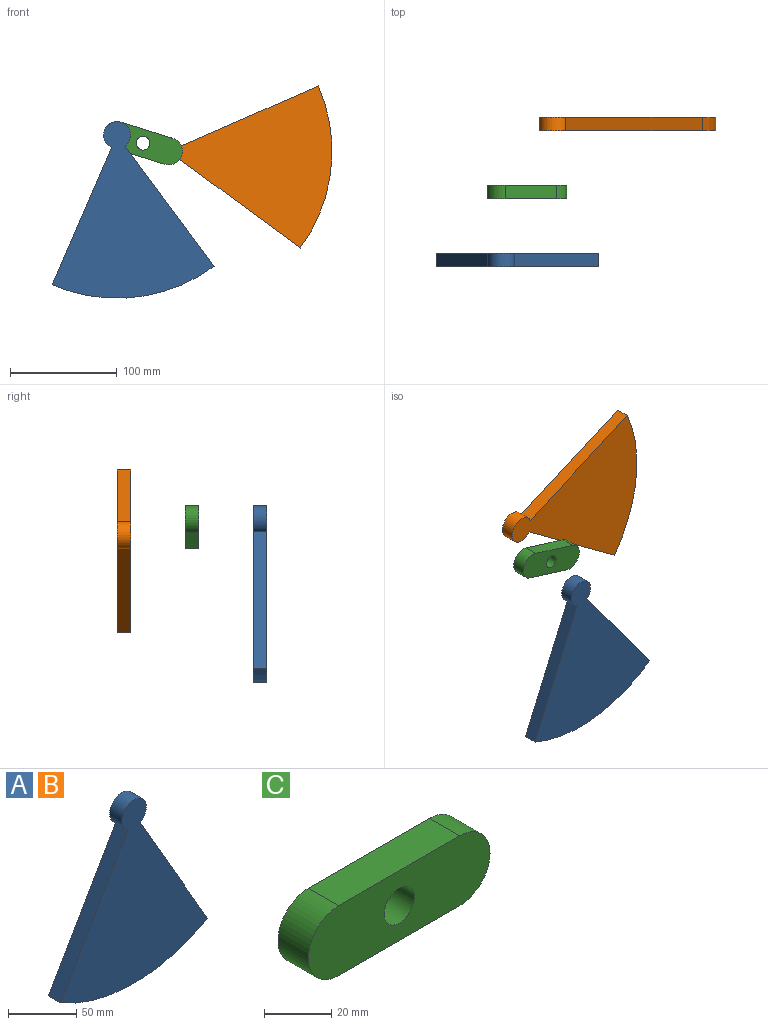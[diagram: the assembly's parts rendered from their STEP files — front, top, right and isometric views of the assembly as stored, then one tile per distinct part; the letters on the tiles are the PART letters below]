
ASSEMBLY  parts=3 mates=2
PART A: 6 faces, bbox 152.4x12.7x165.1 mm
  f0: plane 120.98x69.85mm, normal (-0.87,0,0.5), area 1774.2mm2, adj f2,f3,f4,f5
  f1: plane 120.98x69.85mm, normal (0.87,0,0.5), area 1774.2mm2, adj f2,f3,f4,f5
  f2: cylinder r=152.4mm len=152.4mm, axis (0,1,0), area 2026.8mm2, adj f0,f1,f3,f4
  f3: plane 165.1x152.4mm, normal (0,-1,0), area 12583.2mm2, adj f0,f1,f2,f5
  f4: plane 165.1x152.4mm, normal (0,1,0), area 12583.2mm2, adj f0,f1,f2,f5
  f5: cylinder r=12.7mm len=25.4mm, axis (0,-1,0), area 844.5mm2, adj f0,f1,f3,f4
PART B: same geometry as A
PART C: 7 faces, bbox 76.2x12.7x25.4 mm
  f0: plane 50.8x12.7mm, normal (0,0,1), area 645.2mm2, adj f1,f4,f5,f6
  f1: cylinder r=12.7mm len=25.4mm, axis (0,1,0), area 506.7mm2, adj f0,f2,f5,f6
  f2: plane 50.8x12.7mm, normal (0,0,-1), area 645.2mm2, adj f1,f4,f5,f6
  f3: cylinder r=6.35mm len=12.7mm, axis (0,1,0), area 506.7mm2, adj f5,f6
  f4: cylinder r=12.7mm len=25.4mm, axis (0,1,0), area 506.7mm2, adj f0,f2,f5,f6
  f5: plane 76.2x25.4mm, normal (0,-1,0), area 1670.4mm2, adj f0,f1,f2,f3,f4
  f6: plane 76.2x25.4mm, normal (0,1,0), area 1670.4mm2, adj f0,f1,f2,f3,f4
PLACE A rot(axis=(0,-1,0),6.6deg) t=(-24.26,-63.5,7.52)mm
PLACE B rot(axis=(0,-1,0),83.6deg) t=(24.26,63.5,-7.52)mm
PLACE C rot(axis=(0,1,0),17.2deg) t=(0,0,0)mm
MATE revolute B.f5 <-> C.f4  axis (0,-1,0) through (24.26,57.15,-7.52)mm
MATE revolute A.f2 <-> C.f1  axis (0,1,0) through (-24.26,-57.15,7.52)mm
